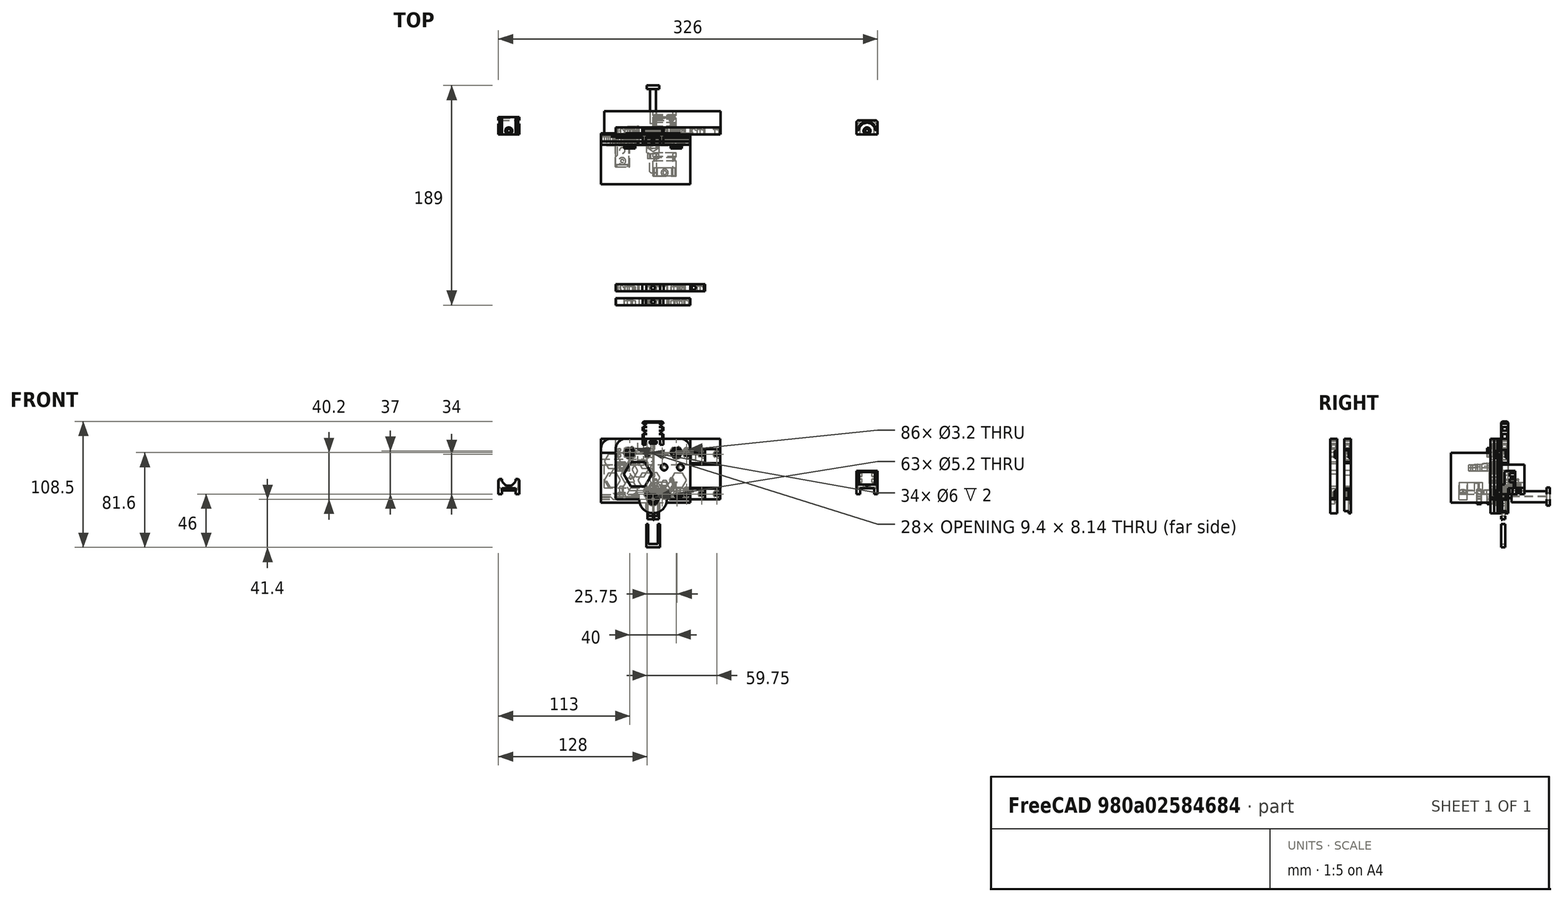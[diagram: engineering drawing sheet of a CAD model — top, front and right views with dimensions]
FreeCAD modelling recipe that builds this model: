
FCSTD DOCUMENT  (FreeCAD 0.18R16146 (Git))
Label: Hemera-mount
License: All rights reserved
LicenseURL: http://en.wikipedia.org/wiki/All_rights_reserved
objects: Part::Feature×109, Part::Box×78, Part::Cut×72, Part::Cylinder×57, Part::MultiFuse×46, Part::Chamfer×32, Part::Fillet×15, Part::MultiCommon×4, Mesh::Feature×1, Sketcher::SketchObject×1, PartDesign::Pad×1, PartDesign::Body×1
note: 417 computed .brp shape members not serialized (recipe doc carries the construction recipe); baked Part::Feature solids carry a one-line shape summary decoded from their .brp

FEATURE [Part::Cylinder] Cylinder018
  Angle = 360
  AttacherType = Attacher::AttachEngine3D
  Height = 9
  Placement = pos=(12,7.9e-15,35.6) rot=(1,0,0;1.5708rad)
  Radius = 2.5
FEATURE [Part::Cylinder] Cylinder020
  Angle = 360
  AttacherType = Attacher::AttachEngine3D
  Height = 5
  Placement = pos=(41.5,6e-15,23.05) rot=(1,0,0;1.5708rad)
  Radius = 2.8
  expr: Radius = 5.6 / 2
FEATURE [Part::Cylinder] Cylinder021
  Angle = 360
  AttacherType = Attacher::AttachEngine3D
  Height = 9
  Placement = pos=(52,8e-15,35.6) rot=(1,0,0;1.5708rad)
  Radius = 2.5
FEATURE [Part::Cylinder] Cylinder022
  Angle = 360
  AttacherType = Attacher::AttachEngine3D
  Height = 9
  Placement = pos=(32,-1e-15,-4.6) rot=(1,0,0;1.5708rad)
  Radius = 2.5
  expr: Radius = 2.5
FEATURE [Part::Cylinder] Cylinder024
  Angle = 360
  AttacherType = Attacher::AttachEngine3D
  Height = 5
  Placement = pos=(55.5,6e-15,23.05) rot=(1,0,0;1.5708rad)
  Radius = 2.8
  expr: Radius = 5.6 / 2
FEATURE [Part::Feature] Pad002  label="nut001"
  Placement = pos=(35,-4,35.6) rot=(1,0,0;1.5708rad)
  shape: bbox 9 x 5 x 7.794 mm, 8 faces (baked)
FEATURE [Part::Feature] Pad003  label="nut002"
  Placement = pos=(75,-4,35.6) rot=(1,0,0;1.5708rad)
  shape: bbox 9 x 5 x 7.794 mm, 8 faces (baked)
FEATURE [Part::Feature] Pad004  label="nut003"
  Placement = pos=(55,-4,-4.6) rot=(1,0,0;1.5708rad)
  shape: bbox 9 x 5 x 7.794 mm, 8 faces (baked)
FEATURE [Part::MultiFuse] Fusion008  label="drill-with-nut"
  Placement = pos=(-32,0,0) rot=(0,0,1;0rad)
  Shapes = -> [Pad004,Pad002,Pad003,Cylinder018,Cylinder020,Cylinder021,Cylinder022,Cylinder024]
FEATURE [Part::Feature] Cut002006  label="FINAL-ender-plate"
  Placement = pos=(-32,0,0) rot=(0,0,1;0rad)
  shape: bbox 64 x 5.5 x 64 mm, 23 faces (baked)
FEATURE [Part::Cylinder] Cylinder
  Angle = 360
  AttacherType = Attacher::AttachEngine3D
  Height = 7
  Placement = pos=(0,-2,-4.6) rot=(1,0,0;1.5708rad)
  Radius = 11.9
FEATURE [Part::Cylinder] Cylinder025
  Angle = 360
  AttacherType = Attacher::AttachEngine3D
  Height = 9
  Placement = pos=(0,0,0) rot=(1,0,0;1.5708rad)
  Radius = 1.5
FEATURE [Part::Cylinder] Cylinder026
  Angle = 360
  AttacherType = Attacher::AttachEngine3D
  Height = 3
  Placement = pos=(0,0,0) rot=(1,0,0;1.5708rad)
  Radius = 3
FEATURE [Part::Box] Box  label="Cube"
  AttacherType = Attacher::AttachEngine3D
  Height = 6
  Length = 3
  Placement = pos=(0,-3,-3) rot=(0,0,1;0rad)
  Width = 3
FEATURE [Part::Cylinder] Cylinder027
  Angle = 360
  AttacherType = Attacher::AttachEngine3D
  Height = 9
  Placement = pos=(-34,0,0) rot=(1,0,0;1.5708rad)
  Radius = 1.5
FEATURE [Part::Cylinder] Cylinder028
  Angle = 360
  AttacherType = Attacher::AttachEngine3D
  Height = 9
  Placement = pos=(-34,8e-15,34) rot=(1,0,0;1.5708rad)
  Radius = 1.5
FEATURE [Part::Cylinder] Cylinder029
  Angle = 360
  AttacherType = Attacher::AttachEngine3D
  Height = 9
  Placement = pos=(0,8e-15,34) rot=(1,0,0;1.5708rad)
  Radius = 1.5
FEATURE [Part::Cylinder] Cylinder030
  Angle = 360
  AttacherType = Attacher::AttachEngine3D
  Height = 3
  Placement = pos=(-34,0,0) rot=(1,0,0;1.5708rad)
  Radius = 3
FEATURE [Part::Cylinder] Cylinder031
  Angle = 360
  AttacherType = Attacher::AttachEngine3D
  Height = 3
  Placement = pos=(-34,8e-15,34) rot=(1,0,0;1.5708rad)
  Radius = 3
FEATURE [Part::Cylinder] Cylinder032
  Angle = 360
  AttacherType = Attacher::AttachEngine3D
  Height = 3
  Placement = pos=(0,8e-15,34) rot=(1,0,0;1.5708rad)
  Radius = 3
FEATURE [Part::Box] Box001  label="Cube001"
  AttacherType = Attacher::AttachEngine3D
  Height = 6
  Length = 3
  Placement = pos=(0,-3,31) rot=(0,0,1;0rad)
  Width = 3
FEATURE [Part::MultiFuse] Fusion  label="hemera-drill"
  Placement = pos=(29,0,1.5) rot=(0,0,1;0rad)
  Shapes = -> [Cylinder025,Cylinder029,Cylinder028,Box,Cylinder030,Cylinder026,Cylinder027,Box001,Cylinder032,Cylinder031]
FEATURE [Part::Box] Box002  label="Cube002"
  AttacherType = Attacher::AttachEngine3D
  Height = 52
  Length = 76.75
  Placement = pos=(-44.75,-9,-4.5) rot=(0,0,1;0rad)
  Width = 7
FEATURE [Part::Box] Box003  label="Cube003"
  AttacherType = Attacher::AttachEngine3D
  Height = 70
  Length = 1
  Placement = pos=(0,0,-22.5) rot=(0,0,1;0rad)
  Width = 1
FEATURE [Part::Box] Box004  label="Cube004"
  AttacherType = Attacher::AttachEngine3D
  Height = 4
  Length = 23.8
  Placement = pos=(-11.9,-9,-4.6) rot=(0,0,1;0rad)
  Width = 7
FEATURE [Part::Box] Box005  label="Cube005"
  AttacherType = Attacher::AttachEngine3D
  Height = 5
  Length = 36.75
  Placement = pos=(-44.75,-9,25) rot=(0,0,1;0rad)
  Width = 3
FEATURE [Part::Box] Box007  label="Cube007"
  AttacherType = Attacher::AttachEngine3D
  Height = 22.5
  Length = 5
  Placement = pos=(-13,-9,25) rot=(0,0,1;0rad)
  Width = 3
FEATURE [Part::Feature] Body001  label="4.7hex"
  shape: bbox 9.4 x 5 x 8.141 mm, 8 faces (baked)
FEATURE [Part::Cylinder] Cylinder033
  Angle = 360
  AttacherType = Attacher::AttachEngine3D
  Height = 9
  Placement = pos=(0,4,-9e-16) rot=(1,0,0;1.5708rad)
  Radius = 2.6
FEATURE [Part::MultiFuse] Fusion009003002  label="big-drill-with-nut"
  Shapes = -> [Body001,Cylinder033]
FEATURE [Part::Feature] Fusion009003002001  label="big-drill-with-nut001"
  Placement = pos=(0,0,-4.6) rot=(0,0,1;0rad)
  shape: bbox 9.4 x 9 x 8.141 mm, 11 faces (baked)
FEATURE [Part::Feature] Fusion009003002002  label="big-drill-with-nut002"
  Placement = pos=(20,0,35.6) rot=(0,0,1;0rad)
  shape: bbox 9.4 x 9 x 8.141 mm, 11 faces (baked)
FEATURE [Part::Feature] Fusion009003002003  label="big-drill-with-nut003"
  Placement = pos=(-20,0,35.6) rot=(0,0,1;0rad)
  shape: bbox 9.4 x 9 x 8.141 mm, 11 faces (baked)
FEATURE [Part::Cylinder] Cylinder034
  Angle = 360
  AttacherType = Attacher::AttachEngine3D
  Height = 5
  Placement = pos=(9.5,4,23.05) rot=(1,0,0;1.5708rad)
  Radius = 2.8
FEATURE [Part::Cylinder] Cylinder035
  Angle = 360
  AttacherType = Attacher::AttachEngine3D
  Height = 5
  Placement = pos=(23.5,4,23.05) rot=(1,0,0;1.5708rad)
  Radius = 2.8
FEATURE [Part::MultiFuse] Fusion009003002004  label="big-drill-with-nut-set"
  Placement = pos=(0,-7,0) rot=(0,0,1;0rad)
  Shapes = -> [Cylinder034,Fusion009003002001,Fusion009003002002,Cylinder035,Fusion009003002003]
FEATURE [Part::Feature] Fusion009003002004001  label="big-drill-with-nut-set001"
  Placement = pos=(0,-4,0) rot=(0,0,1;0rad)
  shape: bbox 51 x 9 x 48.34 mm, 39 faces, 5 solids (baked)
FEATURE [Part::Feature] Fusion009003002004002  label="hemera-drill002"
  Placement = pos=(29,0,1.5) rot=(0,0,1;0rad)
  shape: bbox 40 x 9 x 40 mm, 46 faces, 4 solids (baked)
FEATURE [Part::Cylinder] Cylinder036
  Angle = 360
  AttacherType = Attacher::AttachEngine3D
  Height = 9
  Placement = pos=(-5,0,1.5) rot=(1,0,0;1.5708rad)
  Radius = 1.6
FEATURE [Part::Cylinder] Cylinder037
  Angle = 360
  AttacherType = Attacher::AttachEngine3D
  Height = 9
  Placement = pos=(29,0,1.5) rot=(1,0,0;1.5708rad)
  Radius = 1.6
FEATURE [Part::Cylinder] Cylinder038
  Angle = 360
  AttacherType = Attacher::AttachEngine3D
  Height = 9
  Placement = pos=(29,8e-15,35.5) rot=(1,0,0;1.5708rad)
  Radius = 1.6
FEATURE [Part::Cylinder] Cylinder039
  Angle = 360
  AttacherType = Attacher::AttachEngine3D
  Height = 9
  Placement = pos=(-5,8e-15,35.5) rot=(1,0,0;1.5708rad)
  Radius = 1.6
FEATURE [Part::MultiFuse] Fusion009003002004003  label="big-hemera-drill"
  Shapes = -> [Fusion009003002004002,Cylinder036,Cylinder037,Cylinder038,Cylinder039]
FEATURE [Part::Feature] Fusion009003002004003001  label="big-hemera-drill001"
  shape: bbox 40 x 9 x 40 mm, 56 faces, 4 solids (baked)
FEATURE [Part::Feature] Fusion009003002004003002001  label="hemera-base-plate002"
  shape: bbox 76.75 x 9 x 64 mm, 26 faces (baked)
FEATURE [Part::Cut] Cut002008
  Base = -> Fusion009003002004003002001
  Tool = -> Fusion009003002004001
FEATURE [Part::Cut] Cut002009  label="hemera-base-plate-Cut002009"
  Base = -> Cut002008
  Tool = -> Fusion009003002004003001
FEATURE [Part::Feature] Cut002009001  label="hemera-base-plate-Cut002010"
  shape: bbox 76.75 x 9 x 64 mm, 54 faces (baked)
FEATURE [Part::Box] Box008  label="Cube008"
  AttacherType = Attacher::AttachEngine3D
  Height = 1
  Length = 26.5
  Placement = pos=(-44.75,-9,-3) rot=(0,0,1;0rad)
  Width = 9
FEATURE [Part::Chamfer] Chamfer
  Base = -> Box008
  Edges = 1 edges r=0.9: [Edge6]
FEATURE [Part::Cut] Cut002009002  label="hemera-mount-basic"
  Base = -> Cut002009001
  Tool = -> Chamfer
FEATURE [Part::Box] Box009  label="Cube009"
  AttacherType = Attacher::AttachEngine3D
  Height = 34
  Length = 76.75
  Placement = pos=(-44.75,-43,-3) rot=(0,0,1;0rad)
  Width = 34
FEATURE [Part::Fillet] Fillet
  Base = -> Cut002009002
  Edges = 2 edges r=8.5: [Edge2,Edge38]
FEATURE [Part::Box] Box010  label="Cube010"
  AttacherType = Attacher::AttachEngine3D
  Height = 34
  Length = 40
  Placement = pos=(-8,-43,-3) rot=(0,0,1;0rad)
  Width = 34
FEATURE [Part::Cylinder] Cylinder040
  Angle = 360
  AttacherType = Attacher::AttachEngine3D
  Height = 6
  Placement = pos=(0,0,0) rot=(1,0,0;1.5708rad)
  Radius = 2.6
FEATURE [Part::Cylinder] Cylinder041
  Angle = 360
  AttacherType = Attacher::AttachEngine3D
  Height = 3.5
  Placement = pos=(0,-2.5,1e-15) rot=(1,0,0;1.5708rad)
  Radius = 5.5
FEATURE [Part::MultiFuse] Fusion009003002004003002004  label="front-drill"
  Shapes = -> [Cylinder041,Cylinder040]
FEATURE [Part::Feature] Fusion009003002004003002004001  label="front-drill001"
  Placement = pos=(0,0,-4.6) rot=(0,0,1;0rad)
  shape: bbox 11 x 6 x 11 mm, 5 faces (baked)
FEATURE [Part::Feature] Fusion009003002004003002004002  label="front-drill002"
  Placement = pos=(20,0,35.6) rot=(0,0,1;0rad)
  shape: bbox 11 x 6 x 11 mm, 5 faces (baked)
FEATURE [Part::Feature] Fusion009003002004003002004003  label="front-drill003"
  Placement = pos=(-20,0,35.6) rot=(0,0,1;0rad)
  shape: bbox 11 x 6 x 11 mm, 5 faces (baked)
FEATURE [Part::Feature] Chamfer001
  Placement = pos=(0,1,1.5) rot=(0,0,1;0rad)
  shape: bbox 26.5 x 9 x 1 mm, 7 faces (baked)
FEATURE [Part::Feature] Fusion009003002004003002004004002  label="big-hemera-drill002"
  Placement = pos=(0,0,1.5) rot=(0,0,1;0rad)
  shape: bbox 40 x 9 x 40 mm, 56 faces, 4 solids (baked)
FEATURE [Part::Cylinder] Cylinder042
  Angle = 360
  AttacherType = Attacher::AttachEngine3D
  Height = 6
  Placement = pos=(9.5,5.1e-15,23.05) rot=(1,0,0;1.5708rad)
  Radius = 2.8
FEATURE [Part::Cylinder] Cylinder043
  Angle = 360
  AttacherType = Attacher::AttachEngine3D
  Height = 6
  Placement = pos=(23.5,5.1e-15,23.05) rot=(1,0,0;1.5708rad)
  Radius = 2.8
FEATURE [Part::MultiFuse] Fusion009003002004003002004004003  label="front-drill-set"
  Shapes = -> [Cylinder043,Cylinder042,Fusion009003002004003002004003,Fusion009003002004003002004001,Fusion009003002004003002004002]
FEATURE [Part::Feature] Fusion009003002004003002004004003001  label="front-drill-set001"
  shape: bbox 51.8 x 6 x 51.2 mm, 21 faces, 5 solids (baked)
FEATURE [Part::Box] Box011  label="Cube011"
  AttacherType = Attacher::AttachEngine3D
  Height = 49
  Length = 12.5
  Placement = pos=(-44.75,0,-1.5) rot=(0,0,1;0rad)
  Width = 1
FEATURE [Part::Feature] Fusion009003002004003002004004003002001  label="hemera-base-slim001"
  Placement = pos=(0,3,0) rot=(0,0,1;0rad)
  shape: bbox 76.75 x 6 x 64 mm, 26 faces (baked)
FEATURE [Part::Cut] Cut002009003
  Base = -> Fusion009003002004003002004004003002001
  Tool = -> Fusion009003002004003002004004003001
FEATURE [Part::Cut] Cut002009004
  Base = -> Cut002009003
  Tool = -> Fusion009003002004003002004004002
FEATURE [Part::MultiFuse] Fusion009003002004003002004004003002002
  Shapes = -> [Cut002009004,Box011]
FEATURE [Part::Cut] Cut002009005
  Base = -> Fusion009003002004003002004004003002002
  Tool = -> Chamfer001
FEATURE [Part::Feature] Cut002009005001  label="Cut002009006"
  shape: bbox 76.75 x 7 x 64 mm, 42 faces (baked)
FEATURE [Part::Chamfer] Chamfer002
  Base = -> Cut002009005001
  Edges = 2 edges r=1: [Edge2,Edge46]
FEATURE [Part::Fillet] Fillet001
  Base = -> Chamfer002
  Edges = 2 edges r=8.5: [Edge64,Edge87]
FEATURE [Part::Feature] Fillet001001  label="Fillet002"
  shape: bbox 76.75 x 7 x 64 mm, 46 faces (baked)
FEATURE [Mesh::Feature] HEMERA_MODEL_1__3_  label="HEMERA-MODEL-1-(3)"
  Placement = pos=(45.4,1.8,-24.6) rot=(-0.57735,0.57735,0.57735;4.18879rad)
FEATURE [Part::Box] Box012  label="Cube012"
  AttacherType = Attacher::AttachEngine3D
  Height = 43
  Length = 76.75
  Placement = pos=(-44.75,-43,-7.5) rot=(0,0,1;0rad)
  Width = 34
FEATURE [Part::MultiFuse] Fusion009003002004003002004004003002003  label="hemera-pos"
  Shapes = -> [Box010,Box009,Box012]
FEATURE [Part::Feature] Fusion009003002004003002004004003002004  label="big-drill-with-nut-set002"
  Placement = pos=(0,-6,0) rot=(0,0,1;0rad)
  shape: bbox 51 x 9 x 48.34 mm, 39 faces, 5 solids (baked)
FEATURE [Part::Feature] Fusion009003002004003002004004003002005  label="big-hemera-drill003"
  Placement = pos=(0,-1,-1.5) rot=(0,0,1;0rad)
  shape: bbox 40 x 9 x 40 mm, 56 faces, 4 solids (baked)
FEATURE [Part::Box] Box013  label="Cube013"
  AttacherType = Attacher::AttachEngine3D
  Height = 52
  Length = 12.5
  Placement = pos=(-44.75,-2,-4.5) rot=(0,0,1;0rad)
  Width = 3
FEATURE [Sketcher::SketchObject] Sketch
  MapMode = 5
  Placement = pos=(0,0,0) rot=(1,0,0;1.5708rad)
  Support = -> [XZ_Plane]
  sketch-geometry (7):
    g0: LineSegment StartX=4.7 StartY=0 StartZ=0 EndX=2.35 EndY=4.07032 EndZ=0
    g1: LineSegment StartX=2.35 StartY=4.07032 StartZ=0 EndX=-2.35 EndY=4.07032 EndZ=0
    g2: LineSegment StartX=-2.35 StartY=4.07032 StartZ=0 EndX=-4.7 EndY=9e-16 EndZ=0
    g3: LineSegment StartX=-4.7 StartY=9e-16 StartZ=0 EndX=-2.35 EndY=-4.07032 EndZ=0
    g4: LineSegment StartX=-2.35 StartY=-4.07032 StartZ=0 EndX=2.35 EndY=-4.07032 EndZ=0
    g5: LineSegment StartX=2.35 StartY=-4.07032 StartZ=0 EndX=4.7 EndY=0 EndZ=0
    g6: Circle [constr] CenterX=0 CenterY=0 CenterZ=0 NormalX=0 NormalY=0 NormalZ=1 AngleXU=0 Radius=4.7
  constraints (13):
    c: Coincident(g0,g1)
    c: Coincident(g1,g2)
    c: Coincident(g2,g3)
    c: Coincident(g3,g4)
    c: Coincident(g4,g5)
    c: Coincident(g5,g0)
    c: Equal(g0, g1-g5) x5
    c: PointOnObject(g0,g6)
    c: PointOnObject(g1,g6)
    c: PointOnObject(g2,g6)
    c: PointOnObject(g3,g6)
    c: PointOnObject(g4,g6)
    c: PointOnObject(g5,g6)
FEATURE [PartDesign::Pad] Pad
  Length = 4
  Length2 = 100
  Placement = pos=(0,0,0) rot=(1,0,0;1.5708rad)
  Profile = -> Sketch
  Type = 0
FEATURE [PartDesign::Body] Body
  Group = -> [Sketch,Pad]
  Origin = -> Origin
  Tip = -> Pad
FEATURE [Part::Cylinder] Cylinder044
  Angle = 360
  AttacherType = Attacher::AttachEngine3D
  Height = 10
  Placement = pos=(0,0,0) rot=(1,0,0;1.5708rad)
  Radius = 2.5
FEATURE [Part::Cylinder] Cylinder045
  Angle = 360
  AttacherType = Attacher::AttachEngine3D
  Height = 33
  Placement = pos=(0,0,0) rot=(1,0,0;1.5708rad)
  Radius = 2.5
FEATURE [Part::Cylinder] Cylinder046
  Angle = 360
  AttacherType = Attacher::AttachEngine3D
  Height = 3
  Placement = pos=(0,0,0) rot=(1,0,0;1.5708rad)
  Radius = 5.5
FEATURE [Part::MultiFuse] Fusion009003002004003002004004003002006003
  Placement = pos=(0,42,0) rot=(0,0,1;0rad)
  Shapes = -> [Cylinder046,Cylinder045]
FEATURE [Part::Cut] Cut002009005003002
  Base = -> Body
  Placement = pos=(0,-17,0) rot=(0,0,1;0rad)
  Tool = -> Cylinder044
FEATURE [Part::MultiFuse] Fusion009003002004003002004004003002006004  label="screw-set"
  Shapes = -> [Fusion009003002004003002004004003002006003,Cut002009005003002]
FEATURE [Part::Feature] Fusion009003002004003002004004003002006004001  label="screw-set001"
  Placement = pos=(0,0,-4.6) rot=(0,0,1;0rad)
  shape: bbox 11 x 63 x 11 mm, 15 faces, 2 solids (baked)
FEATURE [Part::Box] Box015  label="Cube015"
  AttacherType = Attacher::AttachEngine3D
  Height = 2
  Length = 6
  Width = 6
FEATURE [Part::Cylinder] Cylinder047
  Angle = 360
  AttacherType = Attacher::AttachEngine3D
  Height = 9
  Placement = pos=(3,3,-2) rot=(0,0,1;0rad)
  Radius = 1.7
FEATURE [Part::Box] Box017  label="Cube017"
  AttacherType = Attacher::AttachEngine3D
  Height = 5.2
  Length = 2
  Placement = pos=(12,-9,-4.5) rot=(0,0,1;0rad)
  Width = 7
FEATURE [Part::Feature] Cut002009005003004003001  label="9mm-basic-v1"
  shape: bbox 76.75 x 10 x 64 mm, 73 faces (baked)
FEATURE [Part::Feature] Cut002009005003004003002  label="9mm-basic002"
  shape: bbox 76.75 x 10 x 64 mm, 73 faces (baked)
FEATURE [Part::Feature] Body002003  label="Body005"
  Placement = pos=(-21,1,18) rot=(0,0,1;0rad)
  shape: bbox 14 x 10 x 12.12 mm, 8 faces (baked)
FEATURE [Part::Feature] Body002005  label="Body007"
  Placement = pos=(-36,1,26) rot=(0,0,1;0rad)
  shape: bbox 14 x 10 x 12.12 mm, 8 faces (baked)
FEATURE [Part::Feature] Body002006  label="Body008"
  Placement = pos=(-36,1,10) rot=(0,0,1;0rad)
  shape: bbox 14 x 10 x 12.12 mm, 8 faces (baked)
FEATURE [Part::Feature] Body002007  label="Body009"
  Placement = pos=(-21,1,2) rot=(0,0,1;0rad)
  shape: bbox 14 x 10 x 12.12 mm, 8 faces (baked)
FEATURE [Part::Feature] Body002008  label="Body010"
  Placement = pos=(-7,1,10) rot=(0,0,1;0rad)
  shape: bbox 14 x 10 x 12.12 mm, 8 faces (baked)
FEATURE [Part::Feature] Body002010  label="Body012"
  Placement = pos=(21,1,10) rot=(0,0,1;0rad)
  shape: bbox 14 x 10 x 12.12 mm, 8 faces (baked)
FEATURE [Part::Feature] Body002011  label="Body013"
  Placement = pos=(-7,1,26) rot=(0,0,1;0rad)
  shape: bbox 14 x 10 x 12.12 mm, 8 faces (baked)
FEATURE [Part::Feature] Body002012  label="Body014"
  Placement = pos=(7,1,2) rot=(0,0,1;0rad)
  shape: bbox 14 x 10 x 12.12 mm, 8 faces (baked)
FEATURE [Part::Box] Box018  label="Cube018"
  AttacherType = Attacher::AttachEngine3D
  Height = 10
  Length = 18
  Placement = pos=(-14,-9,28) rot=(0,0,1;0rad)
  Width = 10
FEATURE [Part::Box] Box019  label="Cube019"
  AttacherType = Attacher::AttachEngine3D
  Height = 10
  Length = 18
  Placement = pos=(0,-9,-6) rot=(0,0,1;0rad)
  Width = 10
FEATURE [Part::Cut] Cut002009005003004003004
  Base = -> Body002012
  Tool = -> Box019
FEATURE [Part::Cut] Cut002009005003004003005
  Base = -> Body002011
  Tool = -> Box018
FEATURE [Part::MultiFuse] Fusion009003002004003002004004003002006004002003002
  Shapes = -> [Body002003,Body002008,Body002010,Cut002009005003004003004,Cut002009005003004003005,Body002005,Body002006,Body002007]
FEATURE [Part::Cut] Cut002009005003004003006
  Base = -> Cut002009005003004003002
  Tool = -> Fusion009003002004003002004004003002006004002003002
FEATURE [Part::Feature] Cut002009005003004003006_rev  label="9mm-cutout-v1"
  shape: bbox 76.75 x 10 x 64 mm, 119 faces (baked)
FEATURE [Part::Cylinder] Cylinder048
  Angle = 360
  AttacherType = Attacher::AttachEngine3D
  Height = 6
  Placement = pos=(0,6,-4.6) rot=(1,0,0;1.5708rad)
  Radius = 11.9
FEATURE [Part::Box] Box020  label="Cube020"
  AttacherType = Attacher::AttachEngine3D
  Height = 52
  Length = 89.75
  Placement = pos=(-32,0,-4.5) rot=(0,0,1;0rad)
  Width = 6
FEATURE [Part::Box] Box021  label="Cube021"
  AttacherType = Attacher::AttachEngine3D
  Height = 4
  Length = 23.8
  Placement = pos=(-11.9,0,-4.6) rot=(0,0,1;0rad)
  Width = 6
FEATURE [Part::Feature] Fusion009003002004003002004004003002006004002003004  label="big-hemera-drill004"
  Placement = pos=(0,-2,-1.5) rot=(0,0,1;0rad)
  shape: bbox 40 x 9 x 40 mm, 56 faces, 4 solids (baked)
FEATURE [Part::Feature] Fusion009003002004003002004004003002006004002003005  label="big-drill-with-nut-set003"
  Placement = pos=(0,-5,0) rot=(0,0,1;0rad)
  shape: bbox 51 x 9 x 48.34 mm, 39 faces, 5 solids (baked)
FEATURE [Part::Feature] Fusion009003002004003002004004003002006004002003003001  label="hemera-6mm-base001"
  shape: bbox 76.75 x 6 x 64 mm, 26 faces (baked)
FEATURE [Part::Box] Box022  label="Cube022"
  AttacherType = Attacher::AttachEngine3D
  Height = 5.2
  Length = 2
  Placement = pos=(12,-9,-4.5) rot=(0,0,1;0rad)
  Width = 6
FEATURE [Part::Box] Box023  label="Cube023"
  AttacherType = Attacher::AttachEngine3D
  Height = 2
  Length = 10
  Placement = pos=(-44.75,-9,-4.5) rot=(0,0,1;0rad)
  Width = 7
FEATURE [Part::Box] Box024  label="Cube024"
  AttacherType = Attacher::AttachEngine3D
  Height = 52
  Length = 12.5
  Placement = pos=(-44.75,-3,-4.5) rot=(0,0,1;0rad)
  Width = 3
FEATURE [Part::Cylinder] Cylinder049
  Angle = 360
  AttacherType = Attacher::AttachEngine3D
  Height = 10
  Placement = pos=(9.5,5.1e-15,23.05) rot=(1,0,0;1.5708rad)
  Radius = 2.8
FEATURE [Part::Cylinder] Cylinder050
  Angle = 360
  AttacherType = Attacher::AttachEngine3D
  Height = 10
  Placement = pos=(23.5,5.1e-15,23.05) rot=(1,0,0;1.5708rad)
  Radius = 2.8
FEATURE [Part::MultiFuse] Fusion009003002004003002004004003002006004002003003004  label="6mm-extra-drill"
  Shapes = -> [Cylinder050,Cylinder049]
FEATURE [Part::Feature] Fusion009003002004003002004004003002006004002003003004001  label="6mm-extra-drill001"
  shape: bbox 19.6 x 10 x 5.6 mm, 6 faces, 2 solids (baked)
FEATURE [Part::MultiFuse] Fusion009003002004003002004004003002006004002003003004002  label="6mm-dril-with-nut-set"
  Shapes = -> [Fusion009003002004003002004004003002006004002003005,Fusion009003002004003002004004003002006004002003003004001]
FEATURE [Part::Feature] Fusion009003002004003002004004003002006004002003003004002001  label="6mm-dril-with-nut-set001"
  shape: bbox 51 x 10 x 48.34 mm, 36 faces, 5 solids (baked)
FEATURE [Part::Chamfer] Chamfer004002  label="under-fan-cutout"
  Base = -> Box023
  Edges = 1 edges r=1.9: [Edge6]
FEATURE [Part::Feature] Chamfer004002001  label="under-fan-cutout001"
  shape: bbox 10 x 7 x 2 mm, 7 faces (baked)
FEATURE [Part::MultiFuse] Fusion009003002004003002004004003002006004002003003004002002  label="extra-screw-bottom"
  Shapes = -> [Cylinder047,Box015]
FEATURE [Part::Feature] Fusion009003002004003002004004003002006004002003003004002002001  label="extra-screw-bottom001"
  Placement = pos=(19,-9,-2.5) rot=(0,0,1;0rad)
  shape: bbox 6 x 6 x 9 mm, 10 faces (baked)
FEATURE [Part::Cylinder] Cylinder051
  Angle = 360
  AttacherType = Attacher::AttachEngine3D
  Height = 9
  Radius = 1.7
FEATURE [Part::Box] Box025  label="Cube025"
  AttacherType = Attacher::AttachEngine3D
  Height = 2
  Length = 6
  Placement = pos=(-3,-3,5) rot=(0,0,1;0rad)
  Width = 6
FEATURE [Part::MultiFuse] Fusion009003002004003002004004003002006004002003003004002002003  label="extra-screw-top"
  Shapes = -> [Cylinder051,Box025]
FEATURE [Part::Feature] Fusion009003002004003002004004003002006004002003003004002002003001  label="extra-screw-top001"
  Placement = pos=(0,-6,38.5) rot=(0,0,1;0rad)
  shape: bbox 6 x 6 x 9 mm, 10 faces (baked)
FEATURE [Part::Box] Box026  label="Cube026"
  AttacherType = Attacher::AttachEngine3D
  Height = 5
  Length = 3
  Placement = pos=(6,-9,42.5) rot=(0,0,1;0rad)
  Width = 6
FEATURE [Part::Box] Box027  label="Cube027"
  AttacherType = Attacher::AttachEngine3D
  Height = 5
  Length = 3
  Placement = pos=(-9,-9,42.5) rot=(0,0,1;0rad)
  Width = 6
FEATURE [Part::MultiFuse] Fusion009003002004003002004004003002006004002003003004002002003002
  Shapes = -> [Box026,Box027]
FEATURE [Part::Feature] Cut002009005003004003013001  label="6mm-base-v1.003"
  shape: bbox 76.75 x 7 x 64 mm, 83 faces (baked)
FEATURE [Part::Fillet] Fillet001003
  Base = -> Cut002009005003004003013001
  Edges = 2 edges r=8.5: [Edge19,Edge71]
FEATURE [Part::Chamfer] Chamfer004002002
  Base = -> Fillet001003
  Edges = 2 edges r=1: [Edge18,Edge132]
FEATURE [Part::MultiFuse] Fusion009003002004003002004004003002006004002003003004002002003003
  Shapes = -> [Box004,Cylinder,Box002]
FEATURE [Part::Feature] Fusion009003002004003002004004003002006004002003003004002002003004  label="big-drill-with-nut-set004"
  Placement = pos=(0,-4,0) rot=(0,0,1;0rad)
  shape: bbox 51 x 9 x 48.34 mm, 39 faces, 5 solids (baked)
FEATURE [Part::Cut] Cut
  Base = -> Fusion009003002004003002004004003002006004002003003004002002003003
  Tool = -> Fusion009003002004003002004004003002006004002003003004002002003004
FEATURE [Part::Cut] Cut002009005003004003013002
  Base = -> Cut
  Tool = -> Fusion009003002004003002004004003002004
FEATURE [Part::Cut] Cut002009005003004003013003
  Base = -> Cut002009005003004003013002
  Tool = -> Fusion009003002004003002004004003002005
FEATURE [Part::Feature] Fusion009003002004003002004004003002006004002003003004002002003005  label="extra-screw-bottom002"
  Placement = pos=(19,-9,-2.5) rot=(0,0,1;0rad)
  shape: bbox 6 x 6 x 9 mm, 10 faces (baked)
FEATURE [Part::Cut] Cut002009005003004003013004
  Base = -> Cut002009005003004003013003
  Tool = -> Fusion009003002004003002004004003002006004002003003004002002003005
FEATURE [Part::Cut] Cut002009005003004003013005
  Base = -> Cut002009005003004003013004
  Tool = -> Box017
FEATURE [Part::Feature] Chamfer004002002002  label="under-fan-cutout002"
  shape: bbox 10 x 7 x 2 mm, 7 faces (baked)
FEATURE [Part::Feature] Chamfer004002002003  label="under-fan-cutout003"
  Placement = pos=(0,3,0) rot=(0,0,1;0rad)
  shape: bbox 10 x 7 x 2 mm, 7 faces (baked)
FEATURE [Part::Feature] Fusion009003002004003002004004003002006004002003003004002002003008  label="extra-screw-top002"
  Placement = pos=(0,-6,38.5) rot=(0,0,1;0rad)
  shape: bbox 6 x 6 x 9 mm, 10 faces (baked)
FEATURE [Part::Feature] Fusion009003002004003002004004003002006004002003003004002002003002001  label="Fusion009003002004003002004004003002006004002003003004002002003008"
  shape: bbox 18 x 6 x 5 mm, 12 faces, 2 solids (baked)
FEATURE [Part::Feature] Fusion009003002004003002004004003002006004002003003004002002003002002  label="Fusion009003002004003002004004003002006004002003003004002002003009"
  Placement = pos=(0,1,0) rot=(0,0,1;0rad)
  shape: bbox 18 x 6 x 5 mm, 12 faces, 2 solids (baked)
FEATURE [Part::MultiFuse] Fusion009003002004003002004004003002006004002003003004002002003002003
  Shapes = -> [Fusion009003002004003002004004003002006004002003003004002002003002002,Fusion009003002004003002004004003002006004002003003004002002003002001]
FEATURE [Part::Feature] Cut002009005003004003013008001  label="7mm-base-v1.003"
  shape: bbox 76.75 x 8 x 64 mm, 87 faces (baked)
FEATURE [Part::Fillet] Fillet001004
  Base = -> Cut002009005003004003013008001
  Edges = 2 edges r=8.5: [Edge57,Edge165]
FEATURE [Part::Chamfer] Chamfer004002002004
  Base = -> Fillet001004
  Edges = 2 edges r=1: [Edge6,Edge172]
FEATURE [Part::Box] Box028  label="Cube028"
  AttacherType = Attacher::AttachEngine3D
  Height = 2
  Length = 20
  Width = 6
FEATURE [Part::Box] Box029  label="Cube029"
  AttacherType = Attacher::AttachEngine3D
  Height = 5
  Length = 2.8
  Placement = pos=(1.1,0,-4.8) rot=(0,0,1;0rad)
  Width = 6
FEATURE [Part::Box] Box030  label="Cube030"
  AttacherType = Attacher::AttachEngine3D
  Height = 5
  Length = 2.8
  Placement = pos=(16.1,0,-4.8) rot=(0,0,1;0rad)
  Width = 6
FEATURE [Part::Cylinder] Cylinder052
  Angle = 360
  AttacherType = Attacher::AttachEngine3D
  Height = 20
  Placement = pos=(10,2e-15,10) rot=(-1,0,0;1.5708rad)
  Radius = 10
FEATURE [Part::Cylinder] Cylinder053
  Angle = 360
  AttacherType = Attacher::AttachEngine3D
  Height = 20
  Placement = pos=(10,2e-15,10) rot=(-1,0,0;1.5708rad)
  Radius = 7
FEATURE [Part::Cut] Cut002009005003004003013008002
  Base = -> Cylinder052
  Tool = -> Cylinder053
FEATURE [Part::Fillet] Fillet001005
  Base = -> Cut002009005003004003013008002
  Edges = 1 edges r=1: [Edge5]
FEATURE [Part::Fillet] Fillet001006
  Base = -> Fillet001005
  Edges = 1 edges r=1: [Edge8]
FEATURE [Part::Box] Box031  label="Cube031"
  AttacherType = Attacher::AttachEngine3D
  Height = 10
  Length = 2
  Width = 6
FEATURE [Part::Box] Box032  label="Cube032"
  AttacherType = Attacher::AttachEngine3D
  Height = 10
  Length = 2
  Placement = pos=(18,0,0) rot=(0,0,1;0rad)
  Width = 6
FEATURE [Part::Box] Box033  label="Cube033"
  AttacherType = Attacher::AttachEngine3D
  Height = 4
  Length = 2
  Placement = pos=(16,0,0) rot=(0,0,1;0rad)
  Width = 6
FEATURE [Part::Box] Box034  label="Cube034"
  AttacherType = Attacher::AttachEngine3D
  Height = 4
  Length = 2
  Placement = pos=(2,0,0) rot=(0,0,1;0rad)
  Width = 6
FEATURE [Part::MultiFuse] Fusion009003002004003002004004003002006004002003003004002002003002004  label="top-mount-base"
  Shapes = -> [Box034,Box033,Box031,Box032,Box030,Box029,Box028]
FEATURE [Part::Box] Box035  label="Cube035"
  AttacherType = Attacher::AttachEngine3D
  Height = 10
  Length = 20
  Placement = pos=(0,0,10) rot=(0,0,1;0rad)
  Width = 20
FEATURE [Part::Cut] Cut002009005003004003013008003
  Base = -> Fillet001006
  Tool = -> Box035
FEATURE [Part::Cylinder] Cylinder054
  Angle = 360
  AttacherType = Attacher::AttachEngine3D
  Height = 3
  Placement = pos=(10,4e-15,10) rot=(-1,0,0;1.5708rad)
  Radius = 10
FEATURE [Part::Cylinder] Cylinder055
  Angle = 360
  AttacherType = Attacher::AttachEngine3D
  Height = 3
  Placement = pos=(10,4e-15,10) rot=(-1,0,0;1.5708rad)
  Radius = 9
FEATURE [Part::Cut] Cut002009005003004003013008004
  Base = -> Cylinder054
  Placement = pos=(0,13,0) rot=(0,0,1;0rad)
  Tool = -> Cylinder055
FEATURE [Part::Cut] Cut002009005003004003013008005
  Base = -> Cut002009005003004003013008003
  Tool = -> Cut002009005003004003013008004
FEATURE [Part::Cylinder] Cylinder056
  Angle = 360
  AttacherType = Attacher::AttachEngine3D
  Height = 3
  Placement = pos=(10,3,1.1) rot=(0,0,1;0rad)
  Radius = 3
FEATURE [Part::Cylinder] Cylinder057
  Angle = 360
  AttacherType = Attacher::AttachEngine3D
  Height = 4
  Placement = pos=(10,3,0) rot=(0,0,1;0rad)
  Radius = 1.6
FEATURE [Part::Feature] Fusion009003002004003002004004003002006004002003003004002002003002005001  label="Fusion009003002004003002004004003002006004002003003004002002003002006"
  shape: bbox 4 x 4 x 4.1 mm, 5 faces (baked)
FEATURE [Part::Feature] Cut002009005003004003013008005001  label="Cut002009005003004003013008006"
  shape: bbox 20 x 20 x 10 mm, 12 faces (baked)
FEATURE [Part::Feature] Fusion009003002004003002004004003002006004002003003004002002003002004001  label="top-mount-base001"
  shape: bbox 20 x 6 x 14.8 mm, 54 faces (baked)
FEATURE [Part::MultiFuse] Fusion009003002004003002004004003002006004002003003004002002003002005002
  Shapes = -> [Cut002009005003004003013008005,Fusion009003002004003002004004003002006004002003003004002002003002004]
FEATURE [Part::MultiFuse] Fusion009003002004003002004004003002006004002003003004002002003002005003
  Shapes = -> [Cylinder056,Cylinder057]
FEATURE [Part::Cut] Cut002009005003004003013008005002  label="BASE-top-mount-base-6mm"
  Base = -> Fusion009003002004003002004004003002006004002003003004002002003002005002
  Tool = -> Fusion009003002004003002004004003002006004002003003004002002003002005003
FEATURE [Part::Box] Box036  label="Cube036"
  AttacherType = Attacher::AttachEngine3D
  Height = 22
  Length = 20
  Placement = pos=(0,0,-6) rot=(0,0,1;0rad)
  Width = 1
FEATURE [Part::Feature] Fusion009003002004003002004004003002006004002003003004002002003002004001001  label="top-mount-base002"
  shape: bbox 20 x 6 x 14.8 mm, 54 faces (baked)
FEATURE [Part::MultiCommon] Common
  Shapes = -> [Fusion009003002004003002004004003002006004002003003004002002003002004001001,Box036]
FEATURE [Part::Feature] Cut002009005003004003013008005002001  label="top-mount-base-6mm001"
  Placement = pos=(0,-6,0) rot=(0,0,1;0rad)
  shape: bbox 20 x 20 x 14.8 mm, 73 faces (baked)
FEATURE [Part::MultiFuse] Fusion009003002004003002004004003002006004002003003004002002003002004001002  label="BASE-top-mount-base-7mm"
  Shapes = -> [Common,Cut002009005003004003013008005002001]
FEATURE [Part::Feature] Cut002009005003004003013008005002002  label="top-mount-base-6mm002"
  shape: bbox 20 x 20 x 14.8 mm, 29 faces (baked)
FEATURE [Part::Feature] Fusion009003002004003002004004003002006004002003003004002002003002004001002001  label="top-mount-base-7mm001"
  Placement = pos=(0,-30,0) rot=(0,0,1;0rad)
  shape: bbox 20 x 20 x 14.8 mm, 30 faces (baked)
FEATURE [Part::Chamfer] Chamfer004002002004002
  Base = -> Cut002009005003004003013008005002002
  Edges = 2 edges r=0.5: [Edge36,Edge37]
FEATURE [Part::Chamfer] Chamfer004002002004003
  Base = -> Fusion009003002004003002004004003002006004002003003004002002003002004001002001
  Edges = 2 edges r=0.5: [Edge45,Edge46]
FEATURE [Part::Feature] Body002013002001  label="hex-24"
  Placement = pos=(68,0,35) rot=(0,0,1;0rad)
  shape: bbox 24 x 10 x 20.78 mm, 8 faces (baked)
FEATURE [Part::Feature] Body002013002002001  label="hex-14"
  Placement = pos=(73,0,7) rot=(0,0,1;0rad)
  shape: bbox 14 x 10 x 12.12 mm, 8 faces (baked)
FEATURE [Part::Feature] Body002013002002003001  label="hex-6"
  Placement = pos=(97,0,-6) rot=(0,0,1;0rad)
  shape: bbox 6 x 10 x 5.196 mm, 8 faces (baked)
FEATURE [Part::Feature] Body002013002002002001  label="hex-10"
  Placement = pos=(101,0,-1) rot=(0,0,1;0rad)
  shape: bbox 10 x 10 x 8.66 mm, 8 faces (baked)
FEATURE [Part::Feature] Body002013002002003002001  label="hex-4"
  Placement = pos=(86,0,4) rot=(0,0,1;0rad)
  shape: bbox 4 x 10 x 3.464 mm, 8 faces (baked)
FEATURE [Part::MultiFuse] Fusion009003002004003002004004003002006004002003003004002002003002004001002002  label="BASE-cut-part"
  Shapes = -> [Body002013002002003002001,Body002013002002002001,Body002013002002003001,Body002013002002001,Body002013002001]
FEATURE [Part::Chamfer] Chamfer004002002004006  label="export-top-mount-6mm"
  Base = -> Chamfer004002002004002
  Edges = 1 edges r=0.9: [Edge42]
FEATURE [Part::Chamfer] Chamfer004002002004007  label="export-top-mount-7mm"
  Base = -> Chamfer004002002004003
  Edges = 1 edges r=0.9: [Edge42]
FEATURE [Part::MultiFuse] Fusion009003002004003002004004003002006004002003003004002002003002004001002003
  Shapes = -> [Chamfer004002002002,Chamfer004002002003]
FEATURE [Part::MultiFuse] Fusion009003002004003002004004003002006004002003003004002002003002004001002004
  Shapes = -> [Cut002009005003004003013005,Box013]
FEATURE [Part::Cut] Cut002009005003004003013008005002003
  Base = -> Fusion009003002004003002004004003002006004002003003004002002003002004001002004
  Tool = -> Fusion009003002004003002004004003002006004002003003004002002003002004001002003
FEATURE [Part::Cut] Cut002009005003004003013008005002004
  Base = -> Cut002009005003004003013008005002003
  Tool = -> Fusion009003002004003002004004003002006004002003003004002002003008
FEATURE [Part::Cut] Cut002009005003004003013008005002005  label="BASE-7mm-v3"
  Base = -> Cut002009005003004003013008005002004
  Tool = -> Fusion009003002004003002004004003002006004002003003004002002003002003
FEATURE [Part::Feature] Chamfer004002002004008  label="under-fan-cutout004"
  Placement = pos=(0,2,0) rot=(0,0,1;0rad)
  shape: bbox 10 x 7 x 2 mm, 7 faces (baked)
FEATURE [Part::MultiFuse] Fusion009003002004003002004004003002006004002003003004002002003002004001002005
  Shapes = -> [Fusion009003002004003002004004003002006004002003003001,Box024]
FEATURE [Part::MultiFuse] Fusion009003002004003002004004003002006004002003003004002002003002004001002006
  Shapes = -> [Chamfer004002001,Chamfer004002002004008]
FEATURE [Part::Cut] Cut002009005003004003013008005002006
  Base = -> Fusion009003002004003002004004003002006004002003003004002002003002004001002005
  Tool = -> Fusion009003002004003002004004003002006004002003003004002001
FEATURE [Part::Cut] Cut002009005003004003013008005002007
  Base = -> Cut002009005003004003013008005002006
  Tool = -> Fusion009003002004003002004004003002006004002003004
FEATURE [Part::Cut] Cut002009005003004003013008005002008
  Base = -> Cut002009005003004003013008005002007
  Tool = -> Box022
FEATURE [Part::Cut] Cut002009005003004003013008005002009
  Base = -> Cut002009005003004003013008005002008
  Tool = -> Fusion009003002004003002004004003002006004002003003004002002001
FEATURE [Part::Cut] Cut002009005003004003013008005002010
  Base = -> Cut002009005003004003013008005002009
  Tool = -> Fusion009003002004003002004004003002006004002003003004002002003002004001002006
FEATURE [Part::Cut] Cut002009005003004003013008005002011
  Base = -> Cut002009005003004003013008005002010
  Tool = -> Fusion009003002004003002004004003002006004002003003004002002003001
FEATURE [Part::Cut] Cut002009005003004003013008005002012  label="BASE-6mm-v3"
  Base = -> Cut002009005003004003013008005002011
  Tool = -> Fusion009003002004003002004004003002006004002003003004002002003002
FEATURE [Part::Feature] Cut002009005003004003013008005002012001  label="BASE-6mm-v004"
  shape: bbox 76.75 x 9 x 64 mm, 83 faces (baked)
FEATURE [Part::Feature] Cut002009005003004003013008005002005001  label="BASE-7mm-v004"
  shape: bbox 76.75 x 10 x 64 mm, 87 faces (baked)
FEATURE [Part::Fillet] Fillet001007
  Base = -> Cut002009005003004003013008005002005001
  Edges = 2 edges r=8.5: [Edge57,Edge165]
FEATURE [Part::Chamfer] Chamfer004002002004009  label="export-7mm-basic-v3"
  Base = -> Fillet001007
  Edges = 2 edges r=1: [Edge6,Edge172]
FEATURE [Part::Fillet] Fillet001008
  Base = -> Cut002009005003004003013008005002012001
  Edges = 2 edges r=8.5: [Edge13,Edge65]
FEATURE [Part::Chamfer] Chamfer004002002004010  label="export-6mm-basic-v3"
  Base = -> Fillet001008
  Edges = 2 edges r=1: [Edge18,Edge132]
FEATURE [Part::Feature] Chamfer004002002004010001  label="export-6mm-basic-v004"
  shape: bbox 76.75 x 9 x 64 mm, 87 faces (baked)
FEATURE [Part::Feature] Chamfer004002002004009001  label="export-7mm-basic-v004"
  shape: bbox 76.75 x 10 x 64 mm, 91 faces (baked)
FEATURE [Part::Feature] Fusion009003002004003002004004003002006004002003003004002002003002004001002002001  label="BASE-cut-part001"
  shape: bbox 58 x 10 x 26.45 mm, 40 faces, 5 solids (baked)
FEATURE [Part::Feature] Fusion009003002004003002004004003002006004002003003004002002003002004001002002002  label="BASE-cut-part002"
  Placement = pos=(0,1,0) rot=(0,0,1;0rad)
  shape: bbox 58 x 10 x 26.45 mm, 40 faces, 5 solids (baked)
FEATURE [Part::Cut] Cut002009005003004003013008005002012002  label="export-6mm-cutout-v3"
  Base = -> Chamfer004002002004010001
  Tool = -> Fusion009003002004003002004004003002006004002003003004002002003002004001002002001
FEATURE [Part::Cut] Cut002009005003004003013008005002012003  label="export-7mm-cutout-v3"
  Base = -> Chamfer004002002004009001
  Tool = -> Fusion009003002004003002004004003002006004002003003004002002003002004001002002002
FEATURE [Part::Feature] Chamfer004002002004009002  label="export-7mm-basic-v005"
  shape: bbox 76.75 x 10 x 64 mm, 91 faces (baked)
FEATURE [Part::Feature] Chamfer004002002004010002  label="export-6mm-basic-v005"
  shape: bbox 76.75 x 9 x 64 mm, 87 faces (baked)
FEATURE [Part::Box] Box037  label="Cube037"
  AttacherType = Attacher::AttachEngine3D
  Height = 73
  Length = 64
  Placement = pos=(-32,-9,-18) rot=(0,0,1;0rad)
  Width = 7
FEATURE [Part::Box] Box038  label="Cube038"
  AttacherType = Attacher::AttachEngine3D
  Height = 73
  Length = 64
  Placement = pos=(-32,-9,-18) rot=(0,0,1;0rad)
  Width = 7
FEATURE [Part::MultiCommon] Common001
  Shapes = -> [Box037,Chamfer004002002004010002]
FEATURE [Part::MultiCommon] Common002
  Shapes = -> [Box038,Chamfer004002002004009002]
FEATURE [Part::Feature] Body002013002002003002002001  label="24mmhex"
  Placement = pos=(71,-2,-7) rot=(0,0,1;0rad)
  shape: bbox 24 x 7 x 20.78 mm, 8 faces (baked)
FEATURE [Part::Feature] Body002013002002003002002002  label="24mmhex001"
  Placement = pos=(71,-2,-7) rot=(0,0,1;0rad)
  shape: bbox 24 x 7 x 20.78 mm, 8 faces (baked)
FEATURE [Part::Fillet] Fillet001009
  Base = -> Common002
  Edges = 1 edges r=8.5: [Edge2]
FEATURE [Part::Chamfer] Chamfer004002002004010003  label="export-7mm-small-v3"
  Base = -> Fillet001009
  Edges = 1 edges r=1: [Edge3]
FEATURE [Part::Fillet] Fillet001010
  Base = -> Common001
  Edges = 1 edges r=8.5: [Edge2]
FEATURE [Part::Chamfer] Chamfer004002002004010004  label="export-6mm-small-v3"
  Base = -> Fillet001010
  Edges = 1 edges r=1: [Edge3]
FEATURE [Part::Feature] Chamfer004002002004010004001  label="export-6mm-small001"
  shape: bbox 64 x 6 x 64 mm, 82 faces (baked)
FEATURE [Part::Feature] Chamfer004002002004010003001  label="export-7mm-small001"
  shape: bbox 64 x 7 x 64 mm, 86 faces (baked)
FEATURE [Part::Cut] Cut002009005003004003013008005002012005  label="export-7mm-small-cutout-v3"
  Base = -> Chamfer004002002004010003001
  Tool = -> Body002013002002003002002002
FEATURE [Part::Box] Box040  label="2020-profile"
  AttacherType = Attacher::AttachEngine3D
  Height = 20
  Length = 100
  Placement = pos=(-42,0,5.4) rot=(0,0,1;0rad)
  Width = 20
FEATURE [Part::Box] Box041  label="2020-profile-cut"
  AttacherType = Attacher::AttachEngine3D
  Height = 22
  Length = 25.75
  Placement = pos=(32,0,4.5) rot=(0,0,1;0rad)
  Width = 6
FEATURE [Part::Feature] Fusion009003002004003002004004003002006004002003003004002002003002004001002002003  label="big-hemera-drill005"
  Placement = pos=(25.75,7,-1.5) rot=(0,0,1;0rad)
  shape: bbox 40 x 9 x 40 mm, 56 faces, 4 solids (baked)
FEATURE [Part::Feature] Fusion009003002004003002004004003002006004002003003004002002003002004001002002004  label="big-drill-with-nut-set005"
  Placement = pos=(0,4,0) rot=(0,0,1;0rad)
  shape: bbox 51 x 9 x 48.34 mm, 39 faces, 5 solids (baked)
FEATURE [Part::Box] Box042  label="Cube039"
  AttacherType = Attacher::AttachEngine3D
  Height = 9
  Length = 25.75
  Placement = pos=(32,0,38.5) rot=(0,0,1;0rad)
  Width = 6
FEATURE [Part::Feature] Fusion009003002004003002004004003002006004002003003004002002003002004001002002006  label="6mm-extra-drill002"
  Placement = pos=(0,9,0) rot=(0,0,1;0rad)
  shape: bbox 19.6 x 10 x 5.6 mm, 6 faces, 2 solids (baked)
FEATURE [Part::Feature] Chamfer004002002004010004002  label="under-fan-cutout005"
  Placement = pos=(22.75,9,0) rot=(0,0,1;0rad)
  shape: bbox 10 x 7 x 2 mm, 7 faces (baked)
FEATURE [Part::Feature] Fusion009003002004003002004004003002006004002003003004002002003002004001002002007  label="extra-screw-top003"
  Placement = pos=(0,3,38.5) rot=(0,0,1;0rad)
  shape: bbox 6 x 6 x 9 mm, 10 faces (baked)
FEATURE [Part::Feature] Fusion009003002004003002004004003002006004002003003004002002003002004001002002008  label="extra-screw-bottom003"
  Placement = pos=(21.75,0,-2.5) rot=(0,0,1;0rad)
  shape: bbox 6 x 6 x 9 mm, 10 faces (baked)
FEATURE [Part::Feature] Fusion009003002004003002004004003002006004002003003004002002003002004001002002009  label="Fusion009003002004003002004004003002006004002003003004002002003002004001002002006"
  Placement = pos=(0,9,0) rot=(0,0,1;0rad)
  shape: bbox 18 x 6 x 5 mm, 12 faces, 2 solids (baked)
FEATURE [Part::MultiFuse] Fusion009003002004003002004004003002006004002003003004002002003002004001002002010  label="center-slot"
  Shapes = -> [Fusion009003002004003002004004003002006004002003003004002002003002004001002002007,Fusion009003002004003002004004003002006004002003003004002002003002004001002002009]
FEATURE [Part::Feature] Fusion009003002004003002004004003002006004002003003004002002003002004001002002010001  label="center-slot001"
  shape: bbox 18 x 6 x 9 mm, 22 faces, 3 solids (baked)
FEATURE [Part::Feature] Fusion009003002004003002004004003002006004002003003004002002003002004001002002010002  label="extra-screw-left"
  Placement = pos=(35,3,29.5) rot=(0,0,1;0rad)
  shape: bbox 6 x 6 x 9 mm, 10 faces (baked)
FEATURE [Part::Box] Box043  label="Cube040"
  AttacherType = Attacher::AttachEngine3D
  Height = 5.1
  Length = 3.2
  Placement = pos=(12.65,0,-4.5) rot=(0,0,1;0rad)
  Width = 6
FEATURE [Part::Box] Box044  label="Cube041"
  AttacherType = Attacher::AttachEngine3D
  Height = 5.1
  Length = 3.2
  Placement = pos=(-9.1,0,42.4) rot=(0,0,1;0rad)
  Width = 6
FEATURE [Part::Box] Box045  label="Cube042"
  AttacherType = Attacher::AttachEngine3D
  Height = 5.1
  Length = 3.2
  Placement = pos=(5.9,0,42.4) rot=(0,0,1;0rad)
  Width = 6
FEATURE [Part::MultiFuse] Fusion009003002004003002004004003002006004002003003004002002003002004001002002010003
  Shapes = -> [Box045,Box044]
FEATURE [Part::Feature] Chamfer004002002004010004003001  label="Chamfer004002002004010004004"
  shape: bbox 76.75 x 6 x 64 mm, 101 faces (baked)
FEATURE [Part::Cylinder] Cylinder058
  Angle = 360
  AttacherType = Attacher::AttachEngine3D
  Height = 2
  Placement = pos=(0,6,-4.6) rot=(1,0,0;1.5708rad)
  Radius = 3.7
FEATURE [Part::Cut] Cut002009005003004003013008005002012017
  Base = -> Chamfer004002002004010004003001
  Tool = -> Cylinder058
FEATURE [Part::Feature] Body002013002002003002002003001  label="Body002013002002003002002004"
  Placement = pos=(0,4,-4.6) rot=(0,0,1;0rad)
  shape: bbox 9.873 x 4 x 11.4 mm, 8 faces (baked)
FEATURE [Part::Cut] Cut002009005003004003013008005002012018
  Base = -> Cut002009005003004003013008005002012017
  Tool = -> Body002013002002003002002003001
FEATURE [Part::Box] Box046  label="Cube043"
  AttacherType = Attacher::AttachEngine3D
  Height = 20
  Length = 0.9
  Placement = pos=(-4.94,0,-21.75) rot=(0,0,1;0rad)
  Width = 4
FEATURE [Part::Box] Box047  label="Cube044"
  AttacherType = Attacher::AttachEngine3D
  Height = 20
  Length = 0.9
  Placement = pos=(4.04,0,-21.75) rot=(0,0,1;0rad)
  Width = 4
FEATURE [Part::Box] Box048  label="Cube045"
  AttacherType = Attacher::AttachEngine3D
  Height = 20
  Length = 0.8
  Placement = pos=(-4.89,0,-21.75) rot=(0,0,1;0rad)
  Width = 3.5
FEATURE [Part::Box] Box049  label="Cube046"
  AttacherType = Attacher::AttachEngine3D
  Height = 20
  Length = 0.8
  Placement = pos=(4.09,0,-21.75) rot=(0,0,1;0rad)
  Width = 3.5
FEATURE [Part::MultiFuse] Fusion009003002004003002004004003002006004002003003004002002003002004001002002010004  label="lock-cut"
  Shapes = -> [Box046,Box047]
FEATURE [Part::Cut] Cut002009005003004003013008005002012019
  Base = -> Cut002009005003004003013008005002012018
  Tool = -> Fusion009003002004003002004004003002006004002003003004002002003002004001002002010004
FEATURE [Part::Box] Box050  label="Cube047"
  AttacherType = Attacher::AttachEngine3D
  Height = 3
  Length = 9.78
  Placement = pos=(-4.89,0,-21.75) rot=(0,0,1;0rad)
  Width = 3.5
FEATURE [Part::MultiFuse] Fusion009003002004003002004004003002006004002003003004002002003002004001002002010005
  Shapes = -> [Box050,Box049,Box048]
FEATURE [Part::Feature] Fusion009003002004003002004004003002006004002003003004002002003002004001002002010005001  label="Fusion009003002004003002004004003002006004002003003004002002003002004001002002010006"
  Placement = pos=(0,0,-24.25) rot=(0,0,1;0rad)
  shape: bbox 9.78 x 3.5 x 20 mm, 10 faces (baked)
FEATURE [Part::Feature] Fusion009003002004003002004004003002006004002003003004002002001001  label="extra-screw-bottom004"
  Placement = pos=(-30,0,-0.5) rot=(0,0,1;0rad)
  shape: bbox 6 x 6 x 9 mm, 10 faces (baked)
FEATURE [Part::Cut] Cut002009005003004003013008005002012020
  Base = -> Cut002009005003004003013008005002012019
  Tool = -> Fusion009003002004003002004004003002006004002003003004002002001001
FEATURE [Part::Box] Box051  label="Cube048"
  AttacherType = Attacher::AttachEngine3D
  Height = 5.1
  Length = 3.2
  Placement = pos=(-16.1,0,-4.5) rot=(0,0,1;0rad)
  Width = 6
FEATURE [Part::Cut] Cut002009005003004003013008005002012021
  Base = -> Cut002009005003004003013008005002012020
  Tool = -> Box051
FEATURE [Part::Feature] Body002013002002003002002003002001  label="Body002013002002003002002003005"
  Placement = pos=(62,6,-14) rot=(0,0,1;0rad)
  shape: bbox 30 x 6 x 25.98 mm, 8 faces (baked)
FEATURE [Part::Cut] Cut002009005003004003013008005002012022
  Base = -> Cut002009005003004003013008005002012021
  Tool = -> Body002013002002003002002003002001
FEATURE [Part::Feature] Cut002009005003004003013008005002012022001  label="Cut002009005003004003013008005002012023"
  shape: bbox 76.75 x 6 x 64 mm, 123 faces (baked)
FEATURE [Part::Cylinder] Cylinder059
  Angle = 360
  AttacherType = Attacher::AttachEngine3D
  Height = 4
  Placement = pos=(0,4,-4.6) rot=(1,0,0;1.5708rad)
  Radius = 6
FEATURE [Part::Cut] Cut002009005003004003013008005002012022002
  Base = -> Cut002009005003004003013008005002012022001
  Tool = -> Cylinder059
FEATURE [Part::Box] Box052  label="Cube049"
  AttacherType = Attacher::AttachEngine3D
  Height = 20
  Length = 1.8
  Placement = pos=(-5.89,0,-46) rot=(0,0,1;0rad)
  Width = 3.5
FEATURE [Part::Box] Box053  label="Cube050"
  AttacherType = Attacher::AttachEngine3D
  Height = 20
  Length = 1.8
  Placement = pos=(4.09,0,-46) rot=(0,0,1;0rad)
  Width = 3.5
FEATURE [Part::Box] Box054  label="Cube051"
  AttacherType = Attacher::AttachEngine3D
  Height = 15
  Length = 2
  Placement = pos=(-6,0,-19) rot=(0,0,1;0rad)
  Width = 4
FEATURE [Part::Box] Box055  label="Cube052"
  AttacherType = Attacher::AttachEngine3D
  Height = 15
  Length = 2
  Placement = pos=(4,0,-19) rot=(0,0,1;0rad)
  Width = 4
FEATURE [Part::Cut] Cut002009005003004003013008005002012022003
  Base = -> Cut002009005003004003013008005002012022002
  Tool = -> Box054
FEATURE [Part::Cut] Cut002009005003004003013008005002012022004
  Base = -> Cut002009005003004003013008005002012022003
  Tool = -> Box055
FEATURE [Part::MultiFuse] Fusion009003002004003002004004003002006004002003003004002002003002004001002002010005002
  Shapes = -> [Box053,Box052,Fusion009003002004003002004004003002006004002003003004002002003002004001002002010005001]
FEATURE [Part::Box] Box056  label="Cube053"
  AttacherType = Attacher::AttachEngine3D
  Height = 9
  Length = 10
  Placement = pos=(-5,0,-18) rot=(0,0,1;0rad)
  Width = 4
FEATURE [Part::Cut] Cut002009005003004003013008005002012022005
  Base = -> Cut002009005003004003013008005002012022004
  Tool = -> Box056
FEATURE [Part::Feature] Cut002009005003004003013008005002012022005001  label="v4-fix3"
  Placement = pos=(0,-135,0) rot=(0,0,1;0rad)
  shape: bbox 76.75 x 6 x 64 mm, 117 faces (baked)
FEATURE [Part::Feature] Body002013002002003002002003002002001  label="Body002013002002003002002003002003"
  Placement = pos=(0,-10,0) rot=(0,0,1;0rad)
  shape: bbox 7.967 x 9.2 x 3.5 mm, 8 faces (baked)
FEATURE [Part::Box] Box057  label="Cube054"
  AttacherType = Attacher::AttachEngine3D
  Height = 3.5
  Length = 11
  Placement = pos=(-5.5,-16,0) rot=(0,0,1;0rad)
  Width = 8
FEATURE [Part::Box] Box058  label="Cube055"
  AttacherType = Attacher::AttachEngine3D
  Height = 3.5
  Length = 6
  Placement = pos=(-3,-33,0) rot=(0,0,1;0rad)
  Width = 22
FEATURE [Part::MultiFuse] Fusion009003002004003002004004003002006004002003003004002002003002004001002002010005003
  Shapes = -> [Box058,Box057]
FEATURE [Part::Cut] Cut002009005003004003013008005002012022005002
  Base = -> Fusion009003002004003002004004003002006004002003003004002002003002004001002002010005003
  Tool = -> Body002013002002003002002003002002001
FEATURE [Part::Chamfer] Chamfer004002002004010004003002
  Base = -> Cut002009005003004003013008005002012022005002
  Edges = 2 edges r=0.5: [Edge29,Edge49]
FEATURE [Part::Chamfer] Chamfer004002002004010004003003
  Base = -> Chamfer004002002004010004003002
  Edges = 2 edges r=0.5: [Edge16,Edge54]
FEATURE [Part::Chamfer] Chamfer004002002004010004003004
  Base = -> Chamfer004002002004010004003003
  Edges = 4 edges r=1: [Edge16,Edge32,Edge49,Edge61]
FEATURE [Part::Feature] Chamfer004002002004010004003004001  label="Chamfer004002002004010004003005"
  shape: bbox 11 x 25 x 3.5 mm, 23 faces (baked)
FEATURE [Part::Box] Box059  label="Cube056"
  AttacherType = Attacher::AttachEngine3D
  Height = 8
  Length = 3
  Width = 6
FEATURE [Part::Box] Box060  label="Cube057"
  AttacherType = Attacher::AttachEngine3D
  Height = 8
  Length = 3
  Placement = pos=(15,0,0) rot=(0,0,1;0rad)
  Width = 6
FEATURE [Part::Box] Box061  label="Cube058"
  AttacherType = Attacher::AttachEngine3D
  Height = 8
  Length = 18
  Placement = pos=(0,0,5) rot=(0,0,1;0rad)
  Width = 15
FEATURE [Part::Cylinder] Cylinder060
  Angle = 360
  AttacherType = Attacher::AttachEngine3D
  Height = 15
  Placement = pos=(9,3e-15,13) rot=(-1,0,0;1.5708rad)
  Radius = 6
FEATURE [Part::Cut] Cut002009005003004003013008005002012022005003
  Base = -> Box061
  Tool = -> Cylinder060
FEATURE [Part::Cylinder] Cylinder061
  Angle = 360
  AttacherType = Attacher::AttachEngine3D
  Height = 10
  Placement = pos=(9,3,0) rot=(0,0,1;0rad)
  Radius = 1.6
FEATURE [Part::Cylinder] Cylinder062
  Angle = 360
  AttacherType = Attacher::AttachEngine3D
  Height = 2
  Placement = pos=(9,3,6.5) rot=(0,0,1;0rad)
  Radius = 3
FEATURE [Part::Fillet] Fillet001012
  Base = -> Cut002009005003004003013008005002012022005003
  Edges = 2 edges r=1: [Edge7,Edge14]
FEATURE [Part::Chamfer] Chamfer004002002004010004003004002
  Base = -> Fillet001012
  Edges = 2 edges r=2: [Edge15,Edge20]
FEATURE [Part::Chamfer] Chamfer004002002004010004003004003
  Base = -> Chamfer004002002004010004003004002
  Edges = 2 edges r=1: [Edge10,Edge26]
FEATURE [Part::Cut] Cut002009005003004003013008005002012022005004
  Base = -> Chamfer004002002004010004003004003
  Tool = -> Cylinder062
FEATURE [Part::Cut] Cut002009005003004003013008005002012022005005
  Base = -> Cut002009005003004003013008005002012022005004
  Tool = -> Cylinder061
FEATURE [Part::Box] Box062  label="Cube059"
  AttacherType = Attacher::AttachEngine3D
  Height = 2
  Length = 18
  Placement = pos=(0,9,12) rot=(0,0,1;0rad)
  Width = 3
FEATURE [Part::Box] Box063  label="Cube060"
  AttacherType = Attacher::AttachEngine3D
  Height = 10
  Length = 1
  Placement = pos=(0,9,3) rot=(0,0,1;0rad)
  Width = 3
FEATURE [Part::Box] Box064  label="Cube061"
  AttacherType = Attacher::AttachEngine3D
  Height = 9
  Length = 1
  Placement = pos=(17,9,4) rot=(0,0,1;0rad)
  Width = 3
FEATURE [Part::Cut] Cut002009005003004003013008005002012022005006
  Base = -> Cut002009005003004003013008005002012022005005
  Tool = -> Box062
FEATURE [Part::Cut] Cut002009005003004003013008005002012022005007
  Base = -> Cut002009005003004003013008005002012022005006
  Tool = -> Box063
FEATURE [Part::Cut] Cut002009005003004003013008005002012022005008
  Base = -> Cut002009005003004003013008005002012022005007
  Tool = -> Box064
FEATURE [Part::Chamfer] Chamfer004002002004010004003004004
  Base = -> Cut002009005003004003013008005002012022005008
  Edges = 2 edges r=1: [Edge60,Edge80]
FEATURE [Part::MultiFuse] Fusion009003002004003002004004003002006004002003003004002002003002004001002002010005004
  Shapes = -> [Chamfer004002002004010004003004001,Box059,Box060,Chamfer004002002004010004003004004]
FEATURE [Part::Box] Box065  label="Cube062"
  AttacherType = Attacher::AttachEngine3D
  Height = 3
  Length = 14
  Placement = pos=(2,11,3) rot=(0,0,1;0rad)
  Width = 3
FEATURE [Part::Chamfer] Chamfer004002002004010004003004005
  Base = -> Box065
  Edges = 1 edges r=2: [Edge9]
  Placement = pos=(0,1,0) rot=(0,0,1;0rad)
FEATURE [Part::Chamfer] Chamfer004002002004010004003004006
  Base = -> Chamfer004002002004010004003004005
  Edges = 3 edges r=0.5: [Edge4,Edge13,Edge14]
FEATURE [Part::MultiFuse] Fusion009003002004003002004004003002006004002003003004002002003002004001002002010005005
  Shapes = -> [Chamfer004002002004010004003004006,Fusion009003002004003002004004003002006004002003003004002002003002004001002002010005004]
FEATURE [Part::Feature] Fusion009003002004003002004004003002006004002003003004002002003002004001002002010005005001  label="Fusion009003002004003002004004003002006004002003003004002002003002004001002002010005006"
  shape: bbox 23.5 x 48 x 13 mm, 69 faces, 2 solids (baked)
FEATURE [Part::Box] Box066  label="Cube063"
  AttacherType = Attacher::AttachEngine3D
  Height = 10
  Length = 19
  Placement = pos=(-10,-36,0) rot=(0,0,1;0rad)
  Width = 33
FEATURE [Part::Cut] Cut002009005003004003013008005002012022005009
  Base = -> Fusion009003002004003002004004003002006004002003003004002002003002004001002002010005005001
  Placement = pos=(-133,0,0) rot=(0,0,1;0rad)
  Tool = -> Box066
FEATURE [Part::Box] Box067  label="Cube064"
  AttacherType = Attacher::AttachEngine3D
  Height = 5
  Length = 3
  Width = 6
FEATURE [Part::Box] Box068  label="Cube065"
  AttacherType = Attacher::AttachEngine3D
  Height = 5
  Length = 3
  Placement = pos=(15,0,0) rot=(0,0,1;0rad)
  Width = 6
FEATURE [Part::Box] Box069  label="Cube066"
  AttacherType = Attacher::AttachEngine3D
  Height = 3
  Length = 18
  Placement = pos=(0,0,5) rot=(0,0,1;0rad)
  Width = 12
FEATURE [Part::Box] Box070  label="Cube067"
  AttacherType = Attacher::AttachEngine3D
  Height = 12
  Length = 18
  Placement = pos=(0,3,8) rot=(0,0,1;0rad)
  Width = 9
FEATURE [Part::Cylinder] Cylinder063
  Angle = 360
  AttacherType = Attacher::AttachEngine3D
  Height = 10
  Placement = pos=(9,3,0) rot=(0,0,1;0rad)
  Radius = 1.6
FEATURE [Part::Cylinder] Cylinder064
  Angle = 360
  AttacherType = Attacher::AttachEngine3D
  Height = 2
  Placement = pos=(9,3,6) rot=(0,0,1;0rad)
  Radius = 3
FEATURE [Part::Cylinder] Cylinder065
  Angle = 360
  AttacherType = Attacher::AttachEngine3D
  Height = 12
  Placement = pos=(9,3,8) rot=(0,0,1;0rad)
  Radius = 7
FEATURE [Part::Cut] Cut002009005003004003013008005002012022005010
  Base = -> Box070
  Tool = -> Cylinder065
FEATURE [Part::Cylinder] Cylinder066
  Angle = 360
  AttacherType = Attacher::AttachEngine3D
  Height = 15
  Placement = pos=(9,3,5) rot=(0,0,1;0rad)
  Radius = 12
FEATURE [Part::Cylinder] Cylinder067
  Angle = 360
  AttacherType = Attacher::AttachEngine3D
  Height = 3
  Placement = pos=(9,3,15) rot=(0,0,1;0rad)
  Radius = 12
FEATURE [Part::Cylinder] Cylinder068
  Angle = 360
  AttacherType = Attacher::AttachEngine3D
  Height = 3
  Placement = pos=(9,3,15) rot=(0,0,1;0rad)
  Radius = 10
FEATURE [Part::Cut] Cut002009005003004003013008005002012022005013
  Base = -> Cylinder067
  Tool = -> Cylinder068
FEATURE [Part::Feature] Cut002009005003004003013008005002012022005013001  label="Cut002009005003004003013008005002012022005014"
  Placement = pos=(0,0,-5) rot=(0,0,1;0rad)
  shape: bbox 24 x 24 x 3 mm, 4 faces (baked)
FEATURE [Part::Fillet] Fillet001013
  Base = -> Box069
  Edges = 1 edges r=1: [Edge10]
FEATURE [Part::Chamfer] Chamfer004002002004010004003004007
  Base = -> Fillet001013
  Edges = 1 edges r=1: [Edge11]
FEATURE [Part::Cut] Cut002009005003004003013008005002012022005013002
  Base = -> Chamfer004002002004010004003004007
  Tool = -> Cylinder063
FEATURE [Part::Cut] Cut002009005003004003013008005002012022005013003
  Base = -> Cut002009005003004003013008005002012022005013002
  Tool = -> Cylinder064
FEATURE [Part::MultiFuse] Fusion009003002004003002004004003002006004002003003004002002003002004001002002010005005002
  Shapes = -> [Cut002009005003004003013008005002012022005013003,Cut002009005003004003013008005002012022005010]
FEATURE [Part::MultiCommon] Common003
  Shapes = -> [Fusion009003002004003002004004003002006004002003003004002002003002004001002002010005005002,Cylinder066]
FEATURE [Part::Cut] Cut002009005003004003013008005002012022005013004
  Base = -> Common003
  Tool = -> Cut002009005003004003013008005002012022005013001
FEATURE [Part::Cut] Cut002009005003004003013008005002012022005013005
  Base = -> Cut002009005003004003013008005002012022005013004
  Tool = -> Cut002009005003004003013008005002012022005013
FEATURE [Part::Chamfer] Chamfer004002002004010004003004008
  Base = -> Cut002009005003004003013008005002012022005013005
  Edges = 5 edges r=1: [Edge47,Edge48,Edge49,Edge50,Edge52]
FEATURE [Part::MultiFuse] Fusion009003002004003002004004003002006004002003003004002002003002004001002002010005005003
  Placement = pos=(175,0,0) rot=(0,0,1;0rad)
  Shapes = -> [Box067,Box068,Chamfer004002002004010004003004008]
FEATURE [Part::Cut] Cut002009005003004003013008005002012004  label="export-6mm-small-cutout-v3"
  Base = -> Chamfer004002002004010004001
  Placement = pos=(0,-138,0) rot=(0,0,1;0rad)
  Tool = -> Body002013002002003002002001
FEATURE [Part::MultiFuse] Fusion009003002004003002004004003002006004002003003004002002003002004001002002010005005004
  Shapes = -> [Box021,Cylinder048,Box020]
FEATURE [Part::Cut] Cut002009005003004003013008005002012022005013006
  Base = -> Fusion009003002004003002004004003002006004002003003004002002003002004001002002010005005004
  Tool = -> Fusion009003002004003002004004003002006004002003003004002002003002004001002002003
FEATURE [Part::Box] Box071  label="Cube068"
  AttacherType = Attacher::AttachEngine3D
  Height = 10
  Length = 10
  Placement = pos=(16,0,28) rot=(0,0,1;0rad)
  Width = 6
FEATURE [Part::MultiFuse] Fusion009003002004003002004004003002006004002003003004002002003002004001002002010005005005
  Shapes = -> [Cut002009005003004003013008005002012022005013006,Box071]
FEATURE [Part::Feature] Fusion009003002004003002004004003002006004002003003004002002003002004001002002010005005005001  label="Fusion009003002004003002004004003002006004002003003004002002003002004001002002010005005006"
  shape: bbox 89.75 x 6 x 64 mm, 23 faces (baked)
FEATURE [Part::Cut] Cut002009005003004003013008005002012022005013007
  Base = -> Fusion009003002004003002004004003002006004002003003004002002003002004001002002010005005005001
  Tool = -> Fusion009003002004003002004004003002006004002003003004002002003002004001002002004
FEATURE [Part::Cut] Cut002009005003004003013008005002012022005013008
  Base = -> Cut002009005003004003013008005002012022005013007
  Tool = -> Fusion009003002004003002004004003002006004002003003004002002003002004001002002006
FEATURE [Part::Cut] Cut002009005003004003013008005002012022005013009
  Base = -> Cut002009005003004003013008005002012022005013008
  Tool = -> Box041
FEATURE [Part::Cut] Cut002009005003004003013008005002012022005013010
  Base = -> Cut002009005003004003013008005002012022005013009
  Tool = -> Box042
FEATURE [Part::Cylinder] Cylinder069
  Angle = 360
  AttacherType = Attacher::AttachEngine3D
  Height = 10
  Placement = pos=(0,4.5,-4) rot=(1,0,0;1.5708rad)
  Radius = 6
FEATURE [Part::Cylinder] Cylinder070
  Angle = 360
  AttacherType = Attacher::AttachEngine3D
  Height = 10
  Placement = pos=(0,7,-4.6) rot=(1,0,0;1.5708rad)
  Radius = 3.6
FEATURE [Part::Cut] Cut002009005003004003013008005002012022005013011
  Base = -> Cut002009005003004003013008005002012022005013010
  Tool = -> Cylinder070
FEATURE [Part::Cut] Cut002009005003004003013008005002012022005013012
  Base = -> Cut002009005003004003013008005002012022005013011
  Tool = -> Cylinder069
FEATURE [Part::Box] Box072  label="Cube069"
  AttacherType = Attacher::AttachEngine3D
  Height = 16
  Length = 12
  Placement = pos=(-6,-1.5,-20) rot=(0,0,1;0rad)
  Width = 6
FEATURE [Part::Cut] Cut002009005003004003013008005002012022005013013
  Base = -> Cut002009005003004003013008005002012022005013012
  Tool = -> Box072
FEATURE [Part::Box] Box073  label="Cube070"
  AttacherType = Attacher::AttachEngine3D
  Height = 4.5
  Length = 13
  Placement = pos=(-32,0,-4.5) rot=(0,0,1;0rad)
  Width = 6
FEATURE [Part::Cut] Cut002009005003004003013008005002012022005013014
  Base = -> Cut002009005003004003013008005002012022005013013
  Tool = -> Box073
FEATURE [Part::Box] Box074  label="Cube071"
  AttacherType = Attacher::AttachEngine3D
  Height = 2
  Length = 7
  Placement = pos=(-19,0,-4.5) rot=(0,0,1;0rad)
  Width = 6
FEATURE [Part::Cut] Cut002009005003004003013008005002012022005013015
  Base = -> Cut002009005003004003013008005002012022005013014
  Tool = -> Box074
FEATURE [Part::Fillet] Fillet001014
  Base = -> Cut002009005003004003013008005002012022005013015
  Edges = 1 edges r=8.5: [Edge105]
FEATURE [Part::Fillet] Fillet001015
  Base = -> Fillet001014
  Edges = 1 edges r=8.5: [Edge35]
FEATURE [Part::Chamfer] Chamfer004002002004010004003004009
  Base = -> Fillet001015
  Edges = 3 edges r=1: [Edge45,Edge70,Edge79]
FEATURE [Part::Chamfer] Chamfer004002002004010004003004010
  Base = -> Chamfer004002002004010004003004009
  Edges = 4 edges r=0.5: [Edge59,Edge66,Edge83,Edge85]
FEATURE [Part::Box] Box075  label="Cube072"
  AttacherType = Attacher::AttachEngine3D
  Height = 15
  Length = 18
  Placement = pos=(-9,0,47.5) rot=(0,0,1;0rad)
  Width = 6
FEATURE [Part::Chamfer] Chamfer004002002004010004003004011
  Base = -> Chamfer004002002004010004003004010
  Edges = 1 edges r=2.4: [Edge76]
FEATURE [Part::Box] Box076  label="Cube073"
  AttacherType = Attacher::AttachEngine3D
  Height = 3
  Length = 12
  Placement = pos=(-32.5,-28,19.8) rot=(0,0,1;0rad)
  Width = 28
FEATURE [Part::Cylinder] Cylinder071
  Angle = 360
  AttacherType = Attacher::AttachEngine3D
  Height = 10
  Placement = pos=(-26.5,-14,17.5) rot=(0,0,1;0rad)
  Radius = 2.4
FEATURE [Part::Cylinder] Cylinder072
  Angle = 360
  AttacherType = Attacher::AttachEngine3D
  Height = 4
  Placement = pos=(-26.5,-5,22.8) rot=(0,0,1;0rad)
  Radius = 3
FEATURE [Part::Cylinder] Cylinder073
  Angle = 360
  AttacherType = Attacher::AttachEngine3D
  Height = 10
  Placement = pos=(-26.5,-23,17.5) rot=(0,0,1;0rad)
  Radius = 1.35
FEATURE [Part::Cylinder] Cylinder074
  Angle = 360
  AttacherType = Attacher::AttachEngine3D
  Height = 10
  Placement = pos=(-26.5,-5,17.5) rot=(0,0,1;0rad)
  Radius = 1.35
FEATURE [Part::Box] Box077  label="Cube074"
  AttacherType = Attacher::AttachEngine3D
  Height = 6
  Length = 2
  Placement = pos=(-32.5,-18,19.8) rot=(0,0,1;0rad)
  Width = 8
FEATURE [Part::Feature] Body002013002002003002002003002002002001  label="Body002013002002003002002003002002003"
  Placement = pos=(-23.5,12,18.8) rot=(0,0,1;0rad)
  shape: bbox 3 x 26 x 3 mm, 5 faces (baked)
FEATURE [Part::Box] Box078  label="Cube075"
  AttacherType = Attacher::AttachEngine3D
  Height = 3
  Length = 2
  Placement = pos=(-9,0,54.5) rot=(0,0,1;0rad)
  Width = 6
FEATURE [Part::Box] Box079  label="Cube076"
  AttacherType = Attacher::AttachEngine3D
  Height = 3
  Length = 2
  Placement = pos=(-9,0,48.5) rot=(0,0,1;0rad)
  Width = 6
FEATURE [Part::MultiFuse] Fusion009003002004003002004004003002006004002003003004002002003002004001002002010005005005002005
  Shapes = -> [Box079,Box078]
FEATURE [Part::Feature] Fusion009003002004003002004004003002006004002003003004002002003002004001002002010005005005002005001  label="Fusion009003002004003002004004003002006004002003003004002002003002004001002002010005005005002006"
  Placement = pos=(16,0,0) rot=(0,0,1;0rad)
  shape: bbox 2 x 6 x 9 mm, 12 faces, 2 solids (baked)
FEATURE [Part::MultiFuse] Fusion009003002004003002004004003002006004002003003004002002003002004001002002010005005005002005002
  Placement = pos=(0,0,3) rot=(0,0,1;0rad)
  Shapes = -> [Fusion009003002004003002004004003002006004002003003004002002003002004001002002010005005005002005001,Fusion009003002004003002004004003002006004002003003004002002003002004001002002010005005005002005]
FEATURE [Part::Feature] Fusion009003002004003002004004003002006004002003003004002002003002004001002002010005005005002001  label="Fusion009003002004003002004004003002006004002003003004002002003002004001002002010005005005003"
  shape: bbox 89.75 x 34 x 64 mm, 70 faces (baked)
FEATURE [Part::Feature] Fusion009003002004003002004004003002006004002003003004002002003002004001002002010005005005002005003001  label="Fusion009003002004003002004004003002006004002003003004002002003002004001002002010005005005002005004"
  shape: bbox 89.75 x 34 x 64 mm, 70 faces (baked)
FEATURE [Part::Feature] Body002013002002003002002003002002002002  label="Body002013002002003002002003002002004"
  Placement = pos=(-32.5,12,18.8) rot=(0,0,1;0rad)
  shape: bbox 3 x 26 x 3 mm, 5 faces (baked)
FEATURE [Part::Feature] Body002013002002003002002003002002002003  label="Body002013002002003002002003002002005"
  Placement = pos=(-29.5,12,18.8) rot=(0,0,1;0rad)
  shape: bbox 3 x 26 x 3 mm, 5 faces (baked)
FEATURE [Part::Cylinder] Cylinder075
  Angle = 360
  AttacherType = Attacher::AttachEngine3D
  Height = 4
  Placement = pos=(-26.5,-23,22.8) rot=(0,0,1;0rad)
  Radius = 3
FEATURE [Part::Feature] Body002013002002003002002003002002002004  label="Body002013002002003002002003002002006"
  Placement = pos=(-26.5,12,18.8) rot=(0,0,1;0rad)
  shape: bbox 3 x 26 x 3 mm, 5 faces (baked)
FEATURE [Part::MultiFuse] Fusion009003002004003002004004003002006004002003003004002002003002004001002002010005005005002005003002  label="screw-cut"
  Shapes = -> [Cylinder075,Cylinder072,Cylinder073,Cylinder071,Cylinder074]
FEATURE [Part::MultiFuse] Fusion009003002004003002004004003002006004002003003004002002003002004001002002010005005005002005003003
  Shapes = -> [Body002013002002003002002003002002002004,Body002013002002003002002003002002002003,Body002013002002003002002003002002002002,Box076,Body002013002002003002002003002002002001]
FEATURE [Part::Feature] Fusion009003002004003002004004003002006004002003003004002002003002004001002002010005005005002005003003001  label="Fusion009003002004003002004004003002006004002003003004002002003002004001002002010005005005002005003004"
  shape: bbox 12 x 28 x 6 mm, 7 faces (baked)
FEATURE [Part::Cut] Cut002009005003004003013008005002012022005013017
  Base = -> Fusion009003002004003002004004003002006004002003003004002002003002004001002002010005005005002005003003001
  Tool = -> Fusion009003002004003002004004003002006004002003003004002002003002004001002002010005005005002005003002
FEATURE [Part::Cut] Cut002009005003004003013008005002012022005013018
  Base = -> Cut002009005003004003013008005002012022005013017
  Tool = -> Box077
FEATURE [Part::Chamfer] Chamfer004002002004010004003004012
  Base = -> Cut002009005003004003013008005002012022005013018
  Edges = 2 edges r=1.95: [Edge6,Edge20]
FEATURE [Part::Chamfer] Chamfer004002002004010004003004013
  Base = -> Chamfer004002002004010004003004012
  Edges = 2 edges r=1.95: [Edge10,Edge40]
FEATURE [Part::Chamfer] Chamfer004002002004010004003004014
  Base = -> Chamfer004002002004010004003004013
  Edges = 1 edges r=0.5: [Edge47]
FEATURE [Part::Cut] Cut002009005003004003013008005002012022005013019
  Base = -> Box075
  Tool = -> Fusion009003002004003002004004003002006004002003003004002002003002004001002002010005005005002005002
FEATURE [Part::Chamfer] Chamfer004002002004010004003004015
  Base = -> Cut002009005003004003013008005002012022005013019
  Edges = 16 edges r=1: [Edge1,Edge3,Edge5,Edge9,Edge13,Edge14,Edge15,Edge19,Edge26,Edge30,Edge34,Edge35,Edge36,Edge40,Edge53,Edge54]
FEATURE [Part::Fillet] Fillet001016
  Base = -> Chamfer004002002004010004003004015
  Edges = 8 edges r=2: [Edge21,Edge25,Edge26,Edge33,Edge38,Edge42,Edge43,Edge50]
FEATURE [Part::Box] Box080  label="Cube077"
  AttacherType = Attacher::AttachEngine3D
  Height = 7
  Length = 4
  Placement = pos=(-32,-4,32) rot=(0,0,1;0rad)
  Width = 5
FEATURE [Part::Box] Box081  label="Cube078"
  AttacherType = Attacher::AttachEngine3D
  Height = 3
  Length = 4
  Placement = pos=(-32,-2,34) rot=(0,0,1;0rad)
  Width = 3
FEATURE [Part::Chamfer] Chamfer004002002004010004003004016
  Base = -> Box080
  Edges = 1 edges r=2: [Edge5]
FEATURE [Part::Cut] Cut002009005003004003013008005002012022005013020
  Base = -> Chamfer004002002004010004003004016
  Tool = -> Box081
FEATURE [Part::Chamfer] Chamfer004002002004010004003004017
  Base = -> Cut002009005003004003013008005002012022005013020
  Edges = 2 edges r=1: [Edge15,Edge19]
FEATURE [Part::Feature] Chamfer004002002004010004003004014001  label="Chamfer004002002004010004003004018"
  Placement = pos=(0,0,2) rot=(0,0,1;0rad)
  shape: bbox 12 x 28 x 6 mm, 24 faces (baked)
FEATURE [Part::MultiFuse] Fusion009003002004003002004004003002006004002003003004002002003002004001002002010005005005002005003003002
  Placement = pos=(0,0.05,0) rot=(0,0,1;0rad)
  Shapes = -> [Chamfer004002002004010004003004014001,Chamfer004002002004010004003004014]
FEATURE [Part::MultiFuse] Fusion009003002004003002004004003002006004002003003004002002003002004001002002010005005005002005003003003
  Shapes = -> [Fusion009003002004003002004004003002006004002003003004002002003002004001002002010005005005002005003003002,Chamfer004002002004010004003004017,Chamfer004002002004010004003004011,Fillet001016]
FEATURE [Part::Feature] Fusion009003002004003002004004003002006004002003003004002002003002004001002002010005005005002005003003003001  label="hemera-mount-aio-v1-fix4"
  shape: bbox 90.25 x 33.95 x 79 mm, 147 faces (baked)
